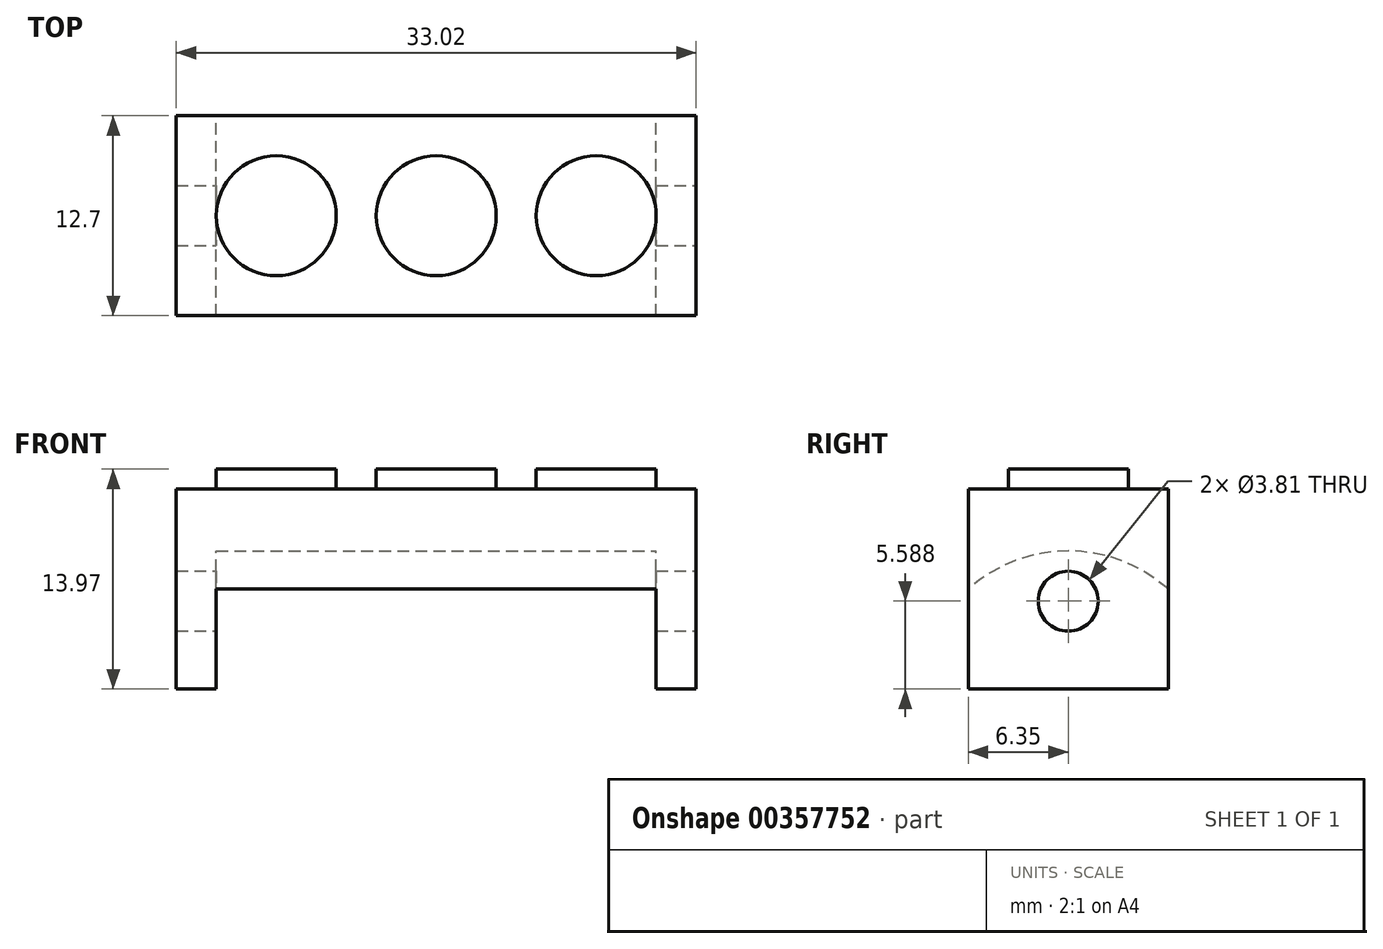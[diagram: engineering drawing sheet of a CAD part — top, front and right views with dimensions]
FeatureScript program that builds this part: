
annotation { "Feature Type Name" : "Feature", "Feature Type Description" : "" }
export const myFeature = defineFeature(function(context is Context, id is Id, definition is map)
    precondition{}
    {
        {
            var Q0;
            Q0=qCreatedBy(makeId("Right.planeOp"),FACE);
            var sketch = newSketch(context, id + "F0", { "sketchPlane" : qUnion([Q0])});
            skLineSegment(sketch, "E0.bottom", {"start": v(-6.35, 6.35) * mm, "end": v(6.35, 6.35) * mm});
            skLineSegment(sketch, "E0.top", {"start": v(-6.35, -6.35) * mm, "end": v(6.35, -6.35) * mm});
            skLineSegment(sketch, "E0.left", {"start": v(-6.35, 6.35) * mm, "end": v(-6.35, -6.35) * mm});
            skLineSegment(sketch, "E0.right", {"start": v(6.35, 6.35) * mm, "end": v(6.35, -6.35) * mm});
            skPoint(sketch, "E0.middle", {"position": v(0, 0) * mm});
            skSolve(sketch);
        }
        {
            var Q0;
            Q0=makeQuery(id+"F0.imprint","IMPRINT",FACE,{"disambiguationData":[TD([[makeQuery(id+"F0.imprint","IMPRINT",EDGE,{"derivedFrom":sQuery(id+"F0.wireOp",EDGE,"E0.bottom")}),-1.0]])]});
            extrude(context, id + "F1", {"entities" : qUnion([Q0]), "depth" : 16.5 * mm, "hasSecondDirection" : true, "secondDirectionOppositeDirection" : true, "secondDirectionDepth" : 16.5 * mm});
        }
        {
            var Q0;
            Q0=makeQuery(id+"F1.opExtrude","SWEPT_FACE",FACE,{"disambiguationData":[OSD([sQuery(id+"F0.wireOp",EDGE,"E0.left")])]});
            var sketch = newSketch(context, id + "F2", { "sketchPlane" : qUnion([Q0])});
            skLineSegment(sketch, "E1.bottom", {"start": v(-13.97, -6.35) * mm, "end": v(13.97, -6.35) * mm});
            skLineSegment(sketch, "E1.top", {"start": v(-13.97, 0) * mm, "end": v(13.97, 0) * mm});
            skLineSegment(sketch, "E1.left", {"start": v(-13.97, -6.35) * mm, "end": v(-13.97, 0) * mm});
            skLineSegment(sketch, "E1.right", {"start": v(13.97, -6.35) * mm, "end": v(13.97, 0) * mm});
            skSolve(sketch);
        }
        {
            var Q0;
            Q0=makeQuery(id+"F2.imprint","IMPRINT",FACE,{"disambiguationData":[TD([[makeQuery(id+"F2.imprint","IMPRINT",EDGE,{"derivedFrom":sQuery(id+"F2.wireOp",EDGE,"E1.bottom")}),-1.0]])]});
            extrude(context, id + "F3", {"entities" : qUnion([Q0]), "operationType" : NewBodyOperationType.REMOVE, "oppositeDirection" : true, "depth" : 25.4 * mm});
        }
        {
            var Q0;
            Q0=makeQuery(id+"F3.boolean.opBoolean","COPY",FACE,{"derivedFrom":makeQuery(id+"F3.opExtrude","SWEPT_FACE",FACE,{"disambiguationData":[OSD([sQuery(id+"F2.wireOp",EDGE,"E1.right")])]})});
            var sketch = newSketch(context, id + "F4", { "sketchPlane" : qUnion([Q0])});
            skArc(sketch, "E2", {"start": v(6.35, 0) * mm, "mid": v(0, 2.43) * mm, "end": v(-6.35, 0) * mm});
            skLineSegment(sketch, "E3", {"start": v(6.35, 0) * mm, "end": v(-6.35, 0) * mm});
            skSolve(sketch);
        }
        {
            var Q0;
            Q0 = qSketchRegion(id + "F4", true);
            extrude(context, id + "F5", {"entities" : qUnion([Q0]), "operationType" : NewBodyOperationType.REMOVE, "depth" : 27.94 * mm});
        }
        {
            var Q0;
            Q0=makeQuery(id+"F1.opExtrude","CAP_FACE",FACE,{"disambiguationData":[OSD([sQuery(id+"F0.wireOp",EDGE,"E0.bottom"),sQuery(id+"F0.wireOp",EDGE,"E0.top"),sQuery(id+"F0.wireOp",EDGE,"E0.left"),sQuery(id+"F0.wireOp",EDGE,"E0.right")])],"isStart":false});
            var sketch = newSketch(context, id + "F6", { "sketchPlane" : qUnion([Q0])});
            skCircle(sketch, "E4", {"center": v(0, -0.76) * mm, "radius": 1.9 * mm});
            skSolve(sketch);
        }
        {
            var Q0;
            Q0=sQuery(id+"F6.wireOp",VERTEX,"E4.center");
            var Q1;
            Q1=makeQuery(id+"F1.opExtrude","SWEPT_BODY",BODY,{"disambiguationData":[OSD([sQuery(id+"F0.wireOp",EDGE,"E0.bottom"),sQuery(id+"F0.wireOp",EDGE,"E0.top"),sQuery(id+"F0.wireOp",EDGE,"E0.left"),sQuery(id+"F0.wireOp",EDGE,"E0.right")])]});
            hole(context, id + "F7", {"style" : HoleStyle.SIMPLE, "endStyle" : HoleEndStyle.THROUGH, "holeDiameter" : 3.8 * mm, "isTappedThrough" : true, "tappedDepth" : 12.7 * mm, "tapClearance" : 3, "locations" : qUnion([Q0]), "scope" : qUnion([Q1])});
        }
        {
            var Q0;
            Q0=makeQuery(id+"F1.opExtrude","SWEPT_FACE",FACE,{"disambiguationData":[OSD([sQuery(id+"F0.wireOp",EDGE,"E0.bottom")])]});
            var sketch = newSketch(context, id + "F8", { "sketchPlane" : qUnion([Q0])});
            skCircle(sketch, "E5", {"center": v(0, 0) * mm, "radius": 3.81 * mm});
            skCircle(sketch, "E6.1.0.0", {"center": v(10.16, 0) * mm, "radius": 3.81 * mm});
            skCircle(sketch, "E7.1.0.0", {"center": v(-10.16, 0) * mm, "radius": 3.81 * mm});
            skSolve(sketch);
        }
        {
            var Q0;
            Q0=makeQuery(id+"F8.imprint","IMPRINT",FACE,{"disambiguationData":[TD([[makeQuery(id+"F8.imprint","IMPRINT",EDGE,{"derivedFrom":sQuery(id+"F8.wireOp",EDGE,"E7.1.0.0")}),1.0]])]});
            var Q1;
            Q1=makeQuery(id+"F8.imprint","IMPRINT",FACE,{"disambiguationData":[TD([[makeQuery(id+"F8.imprint","IMPRINT",EDGE,{"derivedFrom":sQuery(id+"F8.wireOp",EDGE,"E5")}),1.0]])]});
            var Q2;
            Q2=makeQuery(id+"F8.imprint","IMPRINT",FACE,{"disambiguationData":[TD([[makeQuery(id+"F8.imprint","IMPRINT",EDGE,{"derivedFrom":sQuery(id+"F8.wireOp",EDGE,"E6.1.0.0")}),1.0]])]});
            extrude(context, id + "F9", {"entities" : qUnion([Q0, Q1, Q2]), "operationType" : NewBodyOperationType.ADD, "depth" : 1.27 * mm});
        }
    });
